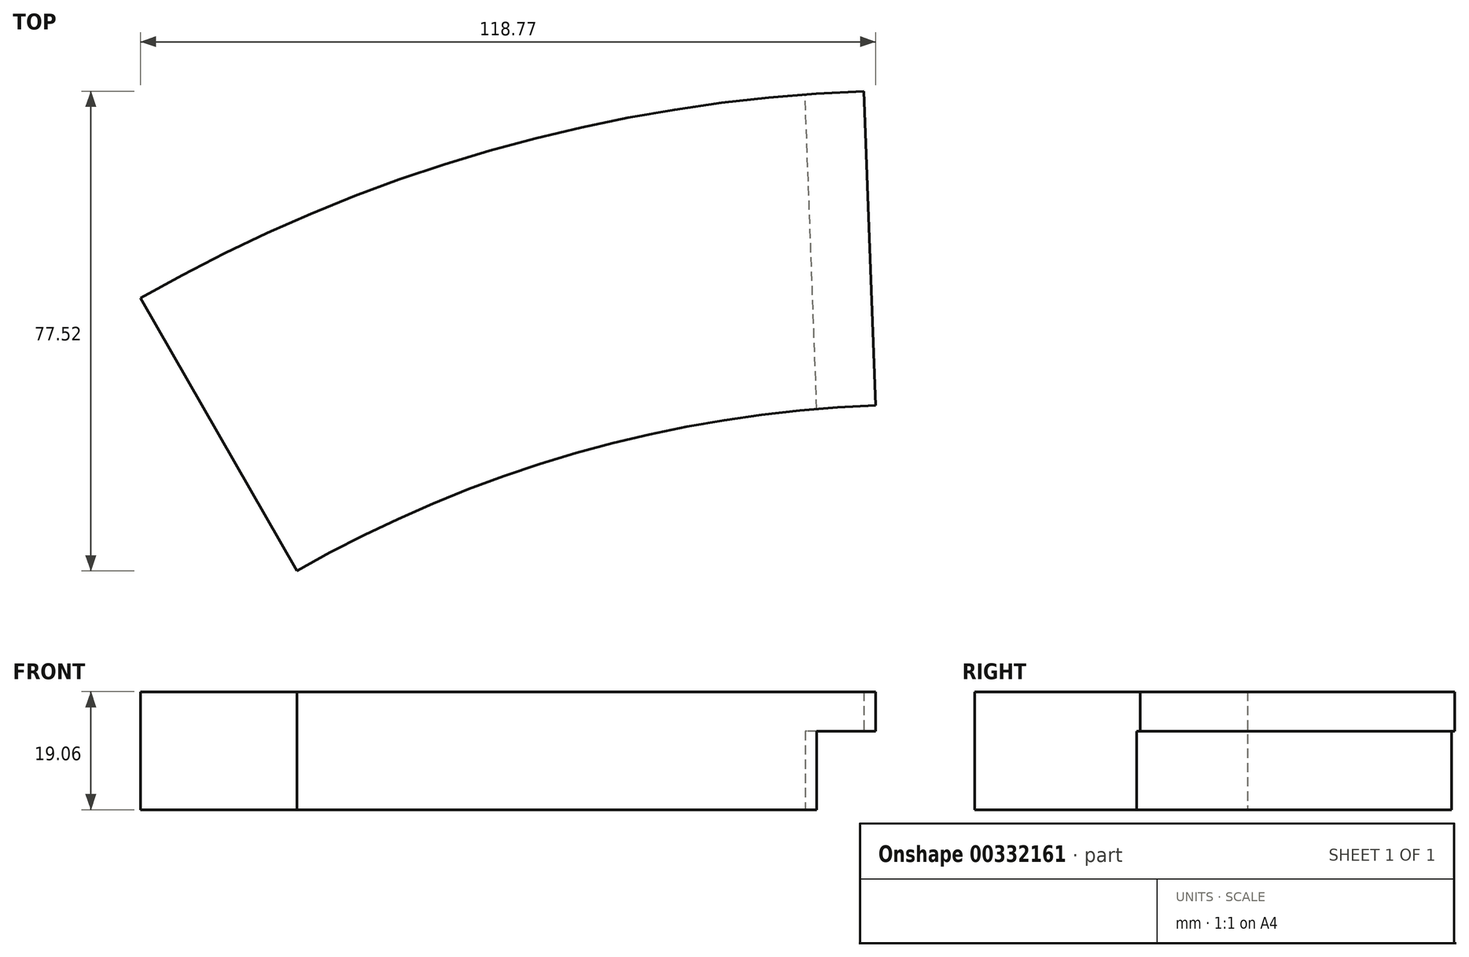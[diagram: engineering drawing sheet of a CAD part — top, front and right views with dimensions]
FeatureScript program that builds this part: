
annotation { "Feature Type Name" : "Feature", "Feature Type Description" : "" }
export const myFeature = defineFeature(function(context is Context, id is Id, definition is map)
    precondition{}
    {
        {
            var Q0;
            Q0=qCreatedBy(makeId("Top.planeOp"),FACE);
            var sketch = newSketch(context, id + "F0", { "sketchPlane" : qUnion([Q0])});
            skCircle(sketch, "E0", {"center": v(0, 0) * mm, "radius": 254 * mm});
            skLineSegment(sketch, "E1", {"start": v(0, 0) * mm, "end": v(-126.3, 220.37) * mm});
            skLineSegment(sketch, "E2.1.0", {"start": v(0, 0) * mm, "end": v(-214.25, 136.43) * mm});
            skLineSegment(sketch, "E2.2.0", {"start": v(0, 0) * mm, "end": v(-253.11, 21.24) * mm});
            skLineSegment(sketch, "E2.3.0", {"start": v(0, 0) * mm, "end": v(-233.99, -98.82) * mm});
            skLineSegment(sketch, "E2.4.0", {"start": v(0, 0) * mm, "end": v(-161.26, -196.24) * mm});
            skLineSegment(sketch, "E2.5.0", {"start": v(0, 0) * mm, "end": v(-51.59, -248.7) * mm});
            skLineSegment(sketch, "E2.6.0", {"start": v(0, 0) * mm, "end": v(69.9, -244.2) * mm});
            skLineSegment(sketch, "E2.7.0", {"start": v(0, 0) * mm, "end": v(175.37, -183.74) * mm});
            skLineSegment(sketch, "E2.8.0", {"start": v(0, 0) * mm, "end": v(240.67, -81.2) * mm});
            skLineSegment(sketch, "E2.9.0", {"start": v(0, 0) * mm, "end": v(250.84, 39.96) * mm});
            skLineSegment(sketch, "E2.10.0", {"start": v(0, 0) * mm, "end": v(203.54, 151.95) * mm});
            skLineSegment(sketch, "E2.11.0", {"start": v(0, 0) * mm, "end": v(109.6, 229.13) * mm});
            skLineSegment(sketch, "E2.12.0", {"start": v(0, 0) * mm, "end": v(-9.43, 253.82) * mm});
            skCircle(sketch, "E3", {"center": v(0, 0) * mm, "radius": 203.2 * mm});
            skSolve(sketch);
        }
        {
            var Q0;
            {var subQ0=sQuery(id+"F0.wireOp",EDGE,"E1");var subQ1=sQuery(id+"F0.wireOp",EDGE,"E0");var subQ2=makeQuery(id+"F0.imprint","INTERSECT",VERTEX,{"derivedFrom":[subQ1,subQ0]});Q0=makeQuery(id+"F0.imprint","IMPRINT",FACE,{"disambiguationData":[TD([[makeQuery(id+"F0.imprint","IMPRINT",EDGE,{"disambiguationData":[TD([[subQ2,1.0]])],"derivedFrom":subQ1}),1.0]])]});}
            extrude(context, id + "F1", {"entities" : qUnion([Q0]), "endBound" : BoundingType.SYMMETRIC, "depth" : 19.05 * mm});
        }
        {
            var Q0;
            Q0=makeQuery(id+"F1.opExtrude","CAP_FACE",FACE,{"disambiguationData":[OSD([sQuery(id+"F0.wireOp",EDGE,"E0"),sQuery(id+"F0.wireOp",EDGE,"E1"),sQuery(id+"F0.wireOp",EDGE,"E2.12.0"),sQuery(id+"F0.wireOp",EDGE,"E3")])],"isStart":true});
            var sketch = newSketch(context, id + "F2", { "sketchPlane" : qUnion([Q0])});
            skLineSegment(sketch, "E4.0", {"start": v(-17.05, -202.48) * mm, "end": v(-18.94, -253.3) * mm});
            skArc(sketch, "E5.0", {"start": v(-9.43, -253.82) * mm, "mid": v(-14.19, -253.6) * mm, "end": v(-18.94, -253.3) * mm});
            skArc(sketch, "E6.0", {"start": v(-7.54, -203.06) * mm, "mid": v(-12.3, -202.83) * mm, "end": v(-17.05, -202.48) * mm});
            skPoint(sketch, "E7.orphan", {"position": v(-101.05, -176.3) * mm});
            skPoint(sketch, "E8.orphan", {"position": v(-126.3, -220.37) * mm});
            skSolve(sketch);
        }
        {
            var Q0;
            Q0=makeQuery(id+"F2.imprint","IMPRINT",FACE,{"disambiguationData":[TD([[makeQuery(id+"F2.imprint","IMPRINT",EDGE,{"derivedFrom":sQuery(id+"F2.wireOp",EDGE,"E4.0")}),1.0]])]});
            extrude(context, id + "F3", {"entities" : qUnion([Q0]), "operationType" : NewBodyOperationType.REMOVE, "oppositeDirection" : true, "depth" : 12.7 * mm});
        }
    });
